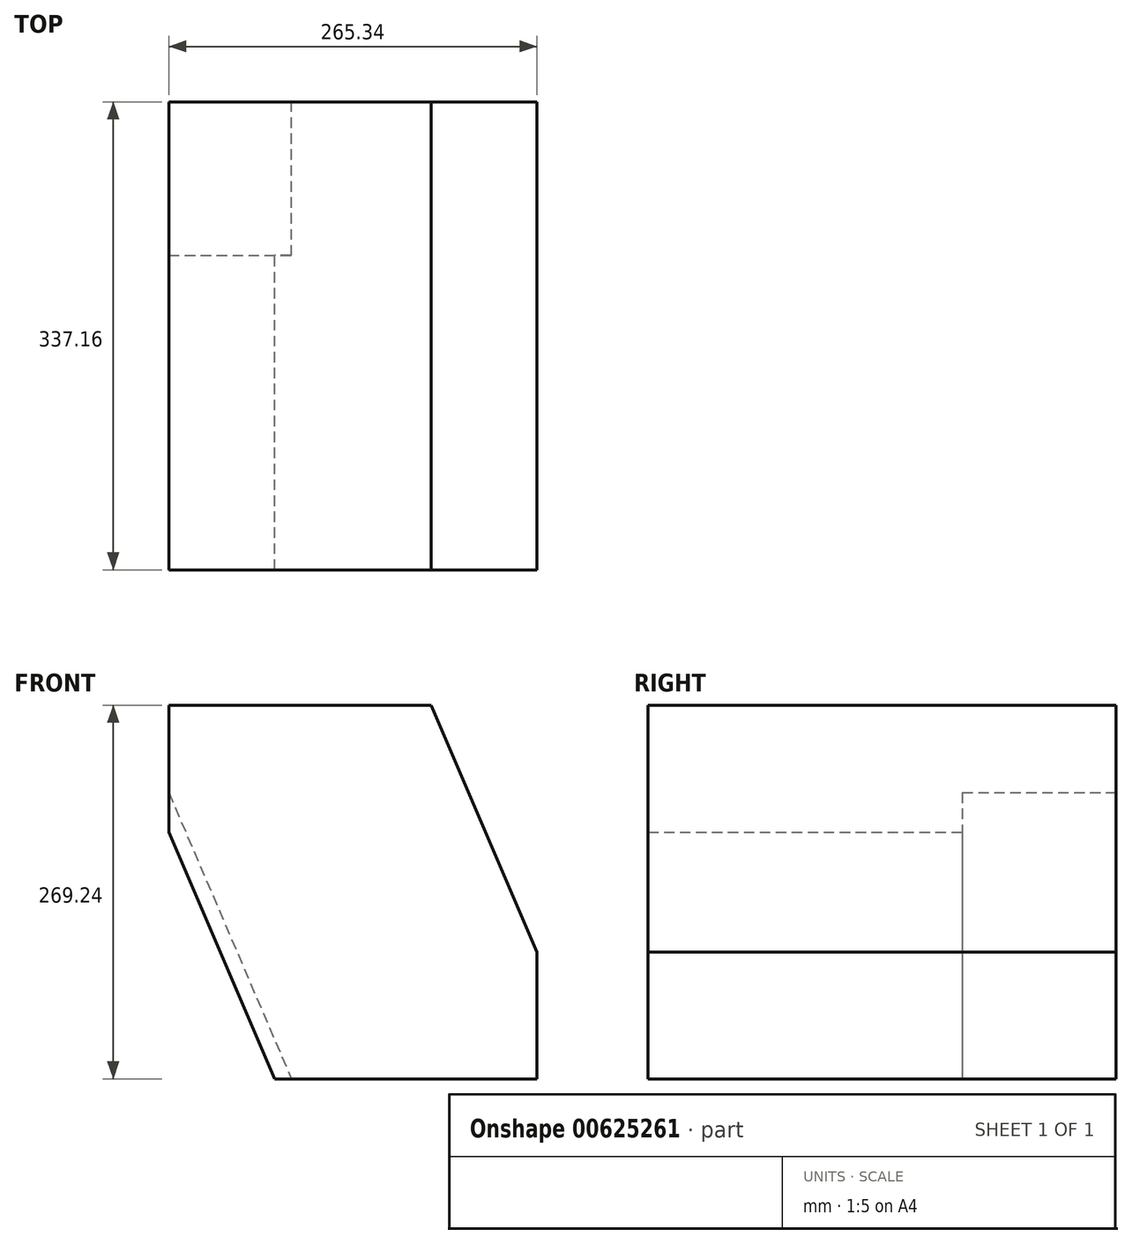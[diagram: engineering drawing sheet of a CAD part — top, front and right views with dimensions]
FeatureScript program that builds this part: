
annotation { "Feature Type Name" : "Feature", "Feature Type Description" : "" }
export const myFeature = defineFeature(function(context is Context, id is Id, definition is map)
    precondition{}
    {
        {
            var Q0;
            Q0=qCreatedBy(makeId("Top.planeOp"),FACE);
            var sketch = newSketch(context, id + "F0", { "sketchPlane" : qUnion([Q0])});
            skLineSegment(sketch, "E0.bottom", {"start": v(132.67, -168.58) * mm, "end": v(-132.67, -168.58) * mm});
            skLineSegment(sketch, "E0.top", {"start": v(132.67, 168.58) * mm, "end": v(-132.67, 168.58) * mm});
            skLineSegment(sketch, "E0.left", {"start": v(132.67, -168.58) * mm, "end": v(132.67, 168.58) * mm});
            skLineSegment(sketch, "E0.right", {"start": v(-132.67, -168.58) * mm, "end": v(-132.67, 168.58) * mm});
            skPoint(sketch, "E0.middle", {"position": v(0, 0) * mm});
            skSolve(sketch);
        }
        {
            var Q0;
            Q0=makeQuery(id+"F0.imprint","IMPRINT",FACE,{"disambiguationData":[TD([[makeQuery(id+"F0.imprint","IMPRINT",EDGE,{"derivedFrom":sQuery(id+"F0.wireOp",EDGE,"E0.bottom")}),-1.0]])]});
            extrude(context, id + "F1", {"entities" : qUnion([Q0]), "depth" : 269.24 * mm, "offsetDistance" : 25.4 * mm});
        }
        {
            var Q0;
            Q0=makeQuery(id+"F1.opExtrude","SWEPT_FACE",FACE,{"disambiguationData":[OSD([sQuery(id+"F0.wireOp",EDGE,"E0.top")])]});
            var sketch = newSketch(context, id + "F2", { "sketchPlane" : qUnion([Q0])});
            skLineSegment(sketch, "E1", {"start": v(132.67, 0) * mm, "end": v(132.67, 177.8) * mm});
            skLineSegment(sketch, "E2", {"start": v(132.67, 177.8) * mm, "end": v(56.47, 0) * mm});
            skLineSegment(sketch, "E3", {"start": v(56.47, 0) * mm, "end": v(132.67, 0) * mm});
            skLineSegment(sketch, "E4", {"start": v(-132.67, 269.24) * mm, "end": v(-56.47, 269.24) * mm});
            skLineSegment(sketch, "E5", {"start": v(-56.47, 269.24) * mm, "end": v(-132.67, 91.44) * mm});
            skLineSegment(sketch, "E6", {"start": v(-132.67, 91.44) * mm, "end": v(-132.67, 269.24) * mm});
            skSolve(sketch);
        }
        {
            var Q0;
            Q0=makeQuery(id+"F2.imprint","IMPRINT",FACE,{"disambiguationData":[TD([[makeQuery(id+"F2.imprint","IMPRINT",EDGE,{"derivedFrom":sQuery(id+"F2.wireOp",EDGE,"E4")}),-1.0]])]});
            var Q1;
            Q1=makeQuery(id+"F2.imprint","IMPRINT",FACE,{"disambiguationData":[TD([[makeQuery(id+"F2.imprint","IMPRINT",EDGE,{"derivedFrom":sQuery(id+"F2.wireOp",EDGE,"E1")}),-1.0]])]});
            extrude(context, id + "F3", {"entities" : qUnion([Q0, Q1]), "operationType" : NewBodyOperationType.REMOVE, "oppositeDirection" : true, "depth" : 346.7 * mm, "offsetDistance" : 25.4 * mm});
        }
        {
            var Q0;
            Q0=makeQuery(id+"F1.opExtrude","SWEPT_FACE",FACE,{"disambiguationData":[OSD([sQuery(id+"F0.wireOp",EDGE,"E0.top")])]});
            var sketch = newSketch(context, id + "F4", { "sketchPlane" : qUnion([Q0])});
            skLineSegment(sketch, "E7", {"start": v(132.67, 206.21) * mm, "end": v(44.29, 0) * mm});
            skLineSegment(sketch, "E8", {"start": v(44.29, 0) * mm, "end": v(56.47, 0) * mm});
            skLineSegment(sketch, "E9", {"start": v(56.47, 0) * mm, "end": v(132.67, 177.8) * mm});
            skLineSegment(sketch, "E10", {"start": v(132.67, 177.8) * mm, "end": v(132.67, 206.21) * mm});
            skSolve(sketch);
        }
        {
            var Q0;
            Q0=makeQuery(id+"F4.imprint","IMPRINT",FACE,{"disambiguationData":[TD([[makeQuery(id+"F4.imprint","IMPRINT",EDGE,{"derivedFrom":sQuery(id+"F4.wireOp",EDGE,"E7")}),1.0]])]});
            extrude(context, id + "F5", {"entities" : qUnion([Q0]), "operationType" : NewBodyOperationType.REMOVE, "oppositeDirection" : true, "depth" : 110.74 * mm, "offsetDistance" : 25.4 * mm});
        }
    });
